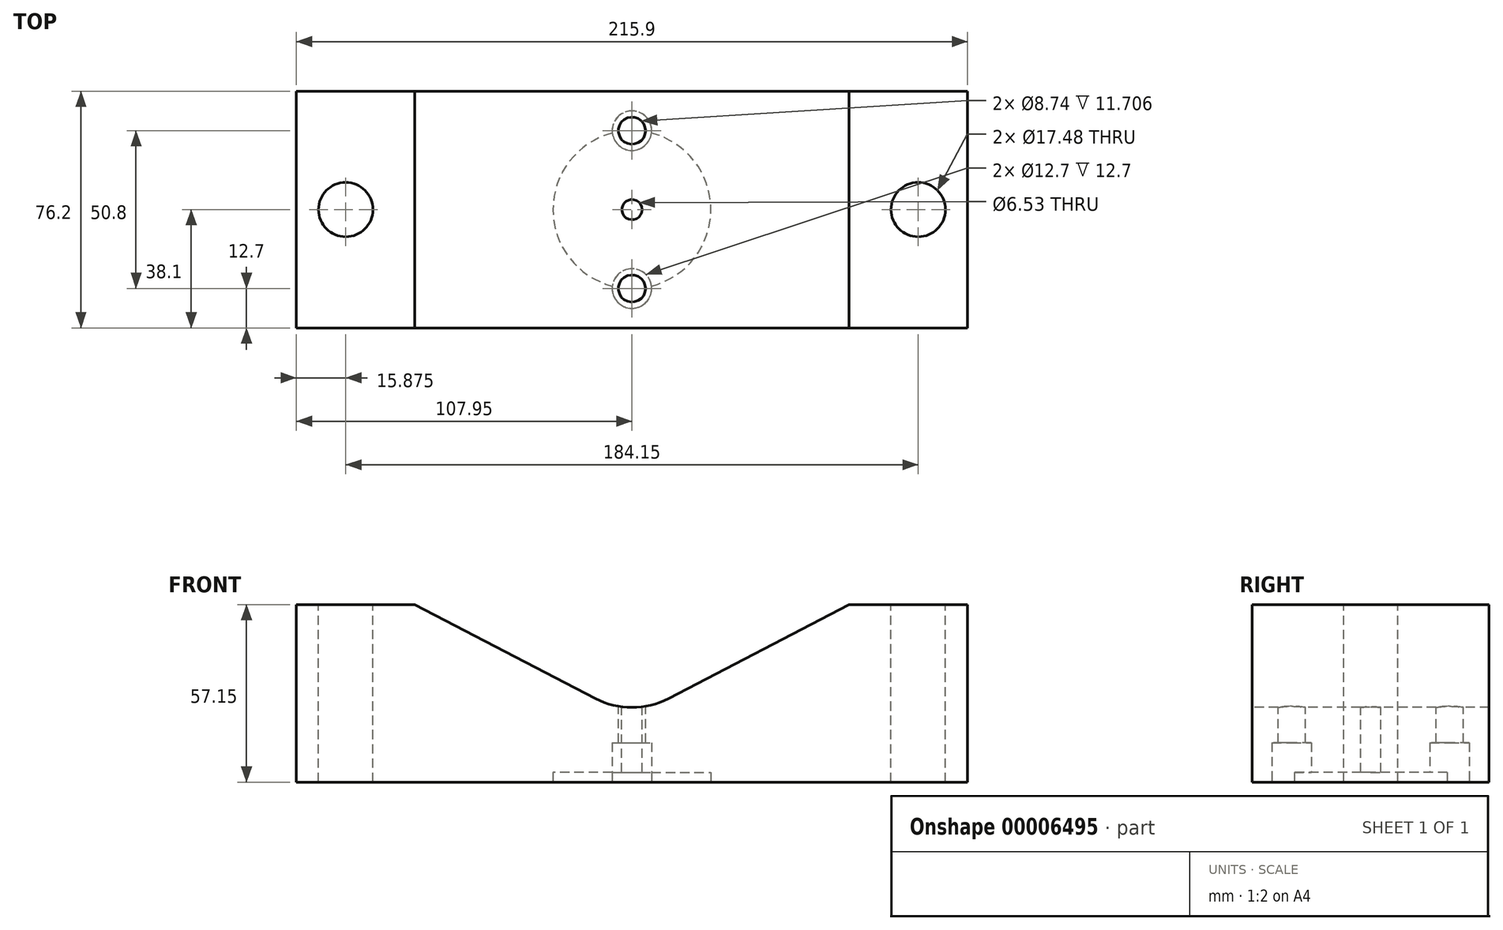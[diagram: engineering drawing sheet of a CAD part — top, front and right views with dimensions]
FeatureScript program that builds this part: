
annotation { "Feature Type Name" : "Feature", "Feature Type Description" : "" }
export const myFeature = defineFeature(function(context is Context, id is Id, definition is map)
    precondition{}
    {
        {
            var Q0;
            Q0=qCreatedBy(makeId("Top.planeOp"),FACE);
            var sketch = newSketch(context, id + "F0", { "sketchPlane" : qUnion([Q0])});
            skLineSegment(sketch, "E0.bottom", {"start": v(0, 0) * mm, "end": v(-215.9, 0) * mm});
            skLineSegment(sketch, "E0.top", {"start": v(0, -76.2) * mm, "end": v(-215.9, -76.2) * mm});
            skLineSegment(sketch, "E0.left", {"start": v(0, 0) * mm, "end": v(0, -76.2) * mm});
            skLineSegment(sketch, "E0.right", {"start": v(-215.9, 0) * mm, "end": v(-215.9, -76.2) * mm});
            skLineSegment(sketch, "E1", {"start": v(-107.95, 0) * mm, "end": v(-107.95, -76.2) * mm, "construction": true});
            skCircle(sketch, "E2", {"center": v(-107.95, -12.7) * mm, "radius": 4.37 * mm});
            skCircle(sketch, "E3", {"center": v(-107.95, -38.1) * mm, "radius": 3.26 * mm});
            skCircle(sketch, "E4", {"center": v(-107.95, -63.5) * mm, "radius": 4.37 * mm});
            skCircle(sketch, "E5", {"center": v(-200.03, -38.1) * mm, "radius": 8.74 * mm});
            skCircle(sketch, "E6", {"center": v(-15.87, -38.1) * mm, "radius": 8.74 * mm});
            skSolve(sketch);
        }
        {
            var Q0;
            Q0=makeQuery(id+"F0.imprint","IMPRINT",FACE,{"disambiguationData":[TD([[makeQuery(id+"F0.imprint","IMPRINT",EDGE,{"derivedFrom":sQuery(id+"F0.wireOp",EDGE,"E0.bottom")}),1.0]])]});
            extrude(context, id + "F1", {"entities" : qUnion([Q0]), "oppositeDirection" : true, "depth" : 57.15 * mm});
        }
        {
            var Q0;
            Q0=makeQuery(id+"F1.opExtrude","CAP_FACE",FACE,{"disambiguationData":[OSD([sQuery(id+"F0.wireOp",EDGE,"E0.bottom"),sQuery(id+"F0.wireOp",EDGE,"E0.top"),sQuery(id+"F0.wireOp",EDGE,"E0.left"),sQuery(id+"F0.wireOp",EDGE,"E0.right"),sQuery(id+"F0.wireOp",EDGE,"E2"),sQuery(id+"F0.wireOp",EDGE,"E3"),sQuery(id+"F0.wireOp",EDGE,"E4"),sQuery(id+"F0.wireOp",EDGE,"E5"),sQuery(id+"F0.wireOp",EDGE,"E6")])],"isStart":false});
            var sketch = newSketch(context, id + "F2", { "sketchPlane" : qUnion([Q0])});
            skCircle(sketch, "E7", {"center": v(-107.95, 63.5) * mm, "radius": 6.35 * mm});
            skCircle(sketch, "E8", {"center": v(-107.95, 12.7) * mm, "radius": 6.35 * mm});
            skSolve(sketch);
        }
        {
            var Q0;
            Q0 = qSketchRegion(id + "F2", true);
            extrude(context, id + "F3", {"entities" : qUnion([Q0]), "operationType" : NewBodyOperationType.REMOVE, "oppositeDirection" : true, "depth" : 12.7 * mm});
        }
        {
            var Q0;
            Q0=makeQuery(id+"F1.opExtrude","SWEPT_FACE",FACE,{"disambiguationData":[OSD([sQuery(id+"F0.wireOp",EDGE,"E0.top")])]});
            var sketch = newSketch(context, id + "F4", { "sketchPlane" : qUnion([Q0])});
            skLineSegment(sketch, "E9", {"start": v(-177.8, 0) * mm, "end": v(-119.68, -30.26) * mm});
            skLineSegment(sketch, "E10", {"start": v(-96.22, -30.26) * mm, "end": v(-38.1, 0) * mm});
            skLineSegment(sketch, "E11", {"start": v(-177.8, 0) * mm, "end": v(-38.1, 0) * mm});
            skPoint(sketch, "E12.visualSharp", {"position": v(-107.95, -36.36) * mm});
            skArc(sketch, "E12.filletArc", {"start": v(-119.68, -30.26) * mm, "mid": v(-107.95, -33.13) * mm, "end": v(-96.22, -30.26) * mm});
            skSolve(sketch);
        }
        {
            var Q0;
            Q0 = qSketchRegion(id + "F4", true);
            extrude(context, id + "F5", {"entities" : qUnion([Q0]), "operationType" : NewBodyOperationType.REMOVE, "endBound" : BoundingType.THROUGH_ALL, "oppositeDirection" : true, "depth" : 25.4 * mm});
        }
        {
            var Q0;
            Q0=makeQuery(id+"F1.opExtrude","CAP_FACE",FACE,{"disambiguationData":[OSD([sQuery(id+"F0.wireOp",EDGE,"E0.bottom"),sQuery(id+"F0.wireOp",EDGE,"E0.top"),sQuery(id+"F0.wireOp",EDGE,"E0.left"),sQuery(id+"F0.wireOp",EDGE,"E0.right"),sQuery(id+"F0.wireOp",EDGE,"E2"),sQuery(id+"F0.wireOp",EDGE,"E3"),sQuery(id+"F0.wireOp",EDGE,"E4"),sQuery(id+"F0.wireOp",EDGE,"E5"),sQuery(id+"F0.wireOp",EDGE,"E6")])],"isStart":false});
            var sketch = newSketch(context, id + "F6", { "sketchPlane" : qUnion([Q0])});
            skCircle(sketch, "E13", {"center": v(-107.95, 38.1) * mm, "radius": 25.4 * mm});
            skSolve(sketch);
        }
        {
            var Q0;
            Q0 = qSketchRegion(id + "F6", true);
            extrude(context, id + "F7", {"entities" : qUnion([Q0]), "operationType" : NewBodyOperationType.REMOVE, "oppositeDirection" : true, "depth" : 3.17 * mm});
        }
    });
